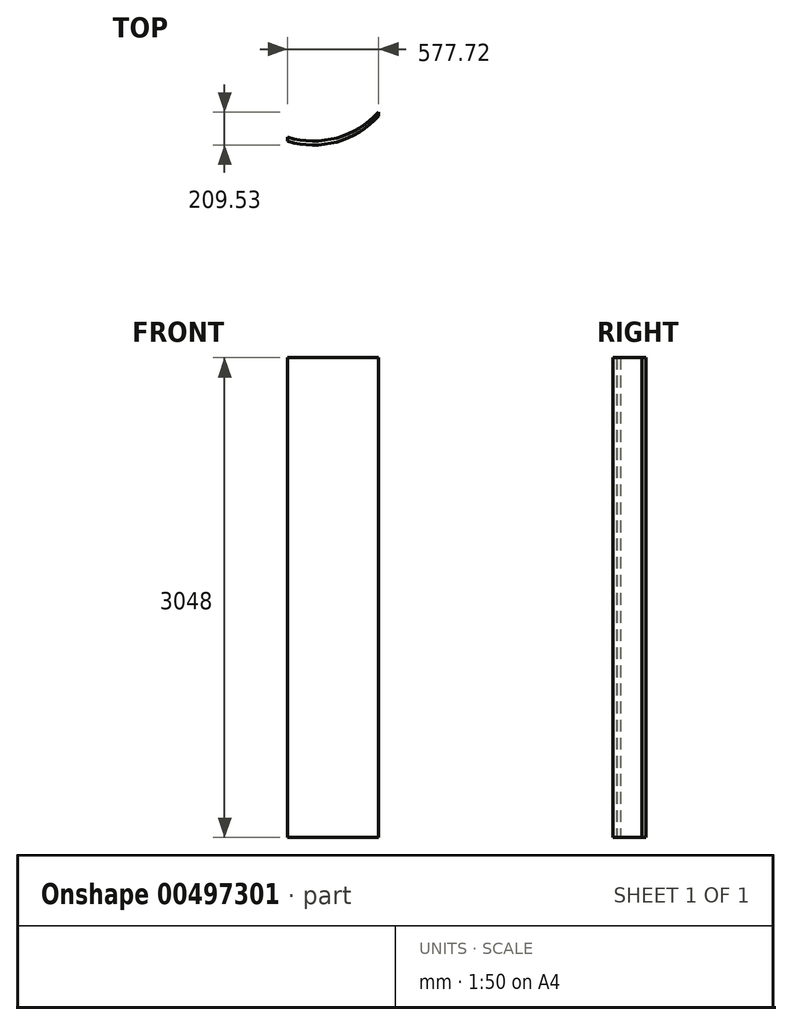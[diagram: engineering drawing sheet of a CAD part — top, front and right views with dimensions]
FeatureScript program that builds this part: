
annotation { "Feature Type Name" : "Feature", "Feature Type Description" : "" }
export const myFeature = defineFeature(function(context is Context, id is Id, definition is map)
    precondition{}
    {
        {
            var Q0;
            Q0=qCreatedBy(makeId("Top.planeOp"),FACE);
            var sketch = newSketch(context, id + "F0", { "sketchPlane" : qUnion([Q0])});
            skArc(sketch, "E0.MirrorCS", {"start": v(-330.57, 11.75) * mm, "mid": v(-18.46, 7.47) * mm, "end": v(247.15, 171.43) * mm});
            skArc(sketch, "E1.MirrorCS", {"start": v(-330.57, 37.15) * mm, "mid": v(-18.46, 32.87) * mm, "end": v(247.15, 196.83) * mm});
            skLineSegment(sketch, "E2", {"start": v(-330.57, 37.15) * mm, "end": v(-330.57, 11.75) * mm});
            skLineSegment(sketch, "E3", {"start": v(247.15, 196.83) * mm, "end": v(247.15, 171.43) * mm});
            skSolve(sketch);
        }
        {
            var Q0;
            Q0=makeQuery(id+"F0.imprint","IMPRINT",FACE,{"disambiguationData":[TD([[makeQuery(id+"F0.imprint","IMPRINT",EDGE,{"derivedFrom":sQuery(id+"F0.wireOp",EDGE,"E0.MirrorCS")}),1.0]])]});
            extrude(context, id + "F1", {"entities" : qUnion([Q0]), "depth" : 3048 * mm});
        }
    });
